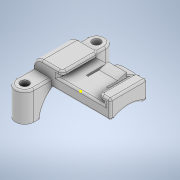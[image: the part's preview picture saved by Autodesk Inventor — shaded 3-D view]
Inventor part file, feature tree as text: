
AUTODESK INVENTOR PART (.ipt)
format: ipt  version: 2020.3 (Build 243373000, 373)  size: 425,984 bytes
history: native  units: mm
features: fillet x11, extrude x7, sketch x7, projected_geometry x1
ambient origin geometry x8: Origin, YZ Plane, XZ Plane, XY Plane, X Axis, Y Axis, Z Axis, Center Point
bodies: Volumenkörper1 (feature_tree)
feature tree (26):
  extrude  "Extrusion1"  Depth=24.0mm
  extrude  "Extrusion2"  Depth=2.0mm
  extrude  "Extrusion3"  Depth=2.0mm
  fillet  "Rundung1"  Radius=20.0mm
  fillet  "Rundung3"  Radius=49.0mm
  fillet  "Rundung4"  Radius=15.8mm
  fillet  "Rundung5"  Radius=32.0mm
  fillet  "Rundung6"  Radius=18.0mm
  extrude  "Extrusion4"  Depth=15.8mm
  extrude  "Extrusion5"  Depth=10.0mm
  sketch  "Skizze6"  dims[d16=10.0mm d17=0.0mm d18=4.5mm]
  extrude  "Extrusion6"  Depth=5.0mm
  fillet  "Rundung10"  Radius=5.0mm
  fillet  "Rundung11"  Radius=5.0mm
  fillet  "Rundung12"  Radius=5.0mm
  fillet  "Rundung13"  [1 undecoded]
  extrude  "Extrusion9"  Depth=1.0mm
  fillet  "Rundung15"  Radius=5.0mm
  fillet  "Rundung16"  Radius=1.0mm
  sketch  "Skizze1"  dims[d0=20.0mm d2=24.0mm]
  sketch  "Skizze2"  dims[d3=32.0mm d4=2.0mm]
  sketch  "Skizze3"  dims[d5=2.0mm d6=2.0mm d7=20.0mm d8=0.0mm d9=49.0mm d10=15.8mm d11=32.0mm d12=18.0mm]
  sketch  "Skizze4"  dims[d14=24.5mm d15=15.8mm]
  sketch  "Skizze7"  dims[d19=4.5mm d20=5.0mm d21=5.0mm d22=5.0mm d23=5.0mm d24=0.0mm d25=0.0mm]
  sketch  "Skizze11"  dims[d26=18.0mm d27=5.0mm d29=5.0mm d30=1.0mm d31=2.0mm d32=1.0mm d33=10.0mm d34=1.0mm d35=1.0mm d36=13.129033mm d37=11.0mm d38=5.0mm d39=10.0mm d40=0.0mm d42=5.0mm d43=2.0mm d44=4.363323mm d45=7.0mm d46=10.0mm d47=0.0mm d48=1.5mm d49=0.0mm d65=1.0mm d66=1.0mm d67=2.0mm d68=0.5mm d73=10.0mm d74=0.0mm d75=10.0mm d76=20.0mm d77=6.0mm d78=1.0mm d79=1.0mm d80=1.5mm d81=0.2mm]
  projected_geometry  "Projizierte Kontur1"
note: 1 required parameter value undecoded (feature->parameter linkage not recoverable at this tier; creation-order binding heuristic only, values carry confidence <= 0.55)
